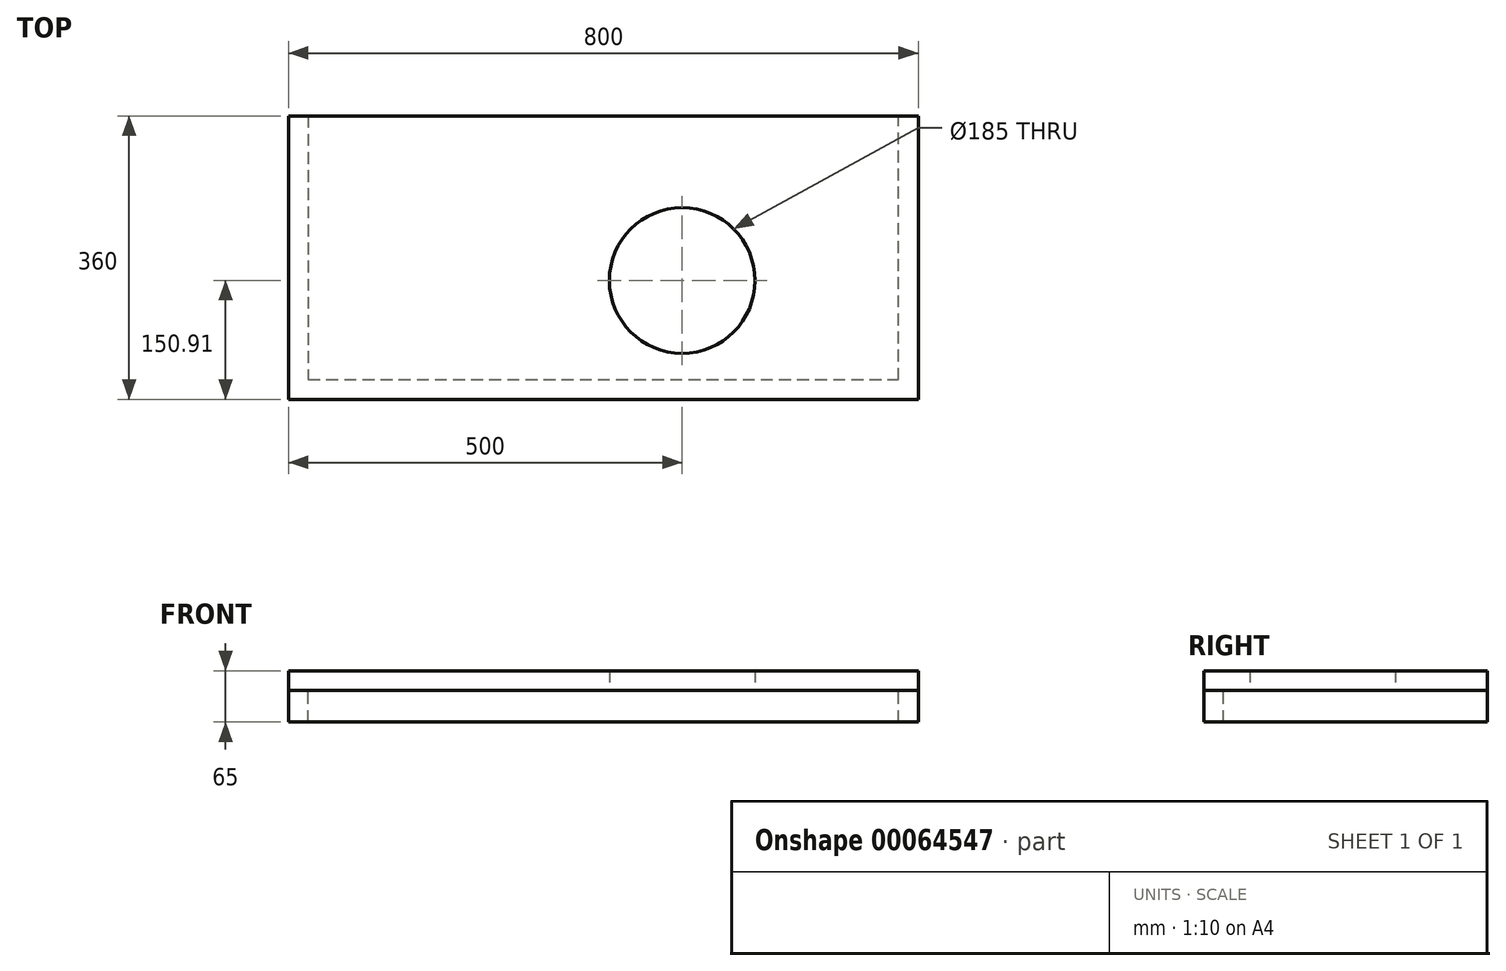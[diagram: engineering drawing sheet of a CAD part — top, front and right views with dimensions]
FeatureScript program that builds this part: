
annotation { "Feature Type Name" : "Feature", "Feature Type Description" : "" }
export const myFeature = defineFeature(function(context is Context, id is Id, definition is map)
    precondition{}
    {
        {
            var Q0;
            Q0=qCreatedBy(makeId("Top.planeOp"),FACE);
            var sketch = newSketch(context, id + "F0", { "sketchPlane" : qUnion([Q0])});
            skLineSegment(sketch, "E0.bottom", {"start": v(0, 0) * mm, "end": v(800, 0) * mm});
            skLineSegment(sketch, "E0.top", {"start": v(0, -360) * mm, "end": v(800, -360) * mm});
            skLineSegment(sketch, "E0.left", {"start": v(0, 0) * mm, "end": v(0, -360) * mm});
            skLineSegment(sketch, "E0.right", {"start": v(800, 0) * mm, "end": v(800, -360) * mm});
            skCircle(sketch, "E1", {"center": v(500, -209.1) * mm, "radius": 92.5 * mm});
            skSolve(sketch);
        }
        {
            var Q0;
            Q0=makeQuery(id+"F0.imprint","IMPRINT",FACE,{"disambiguationData":[TD([[makeQuery(id+"F0.imprint","IMPRINT",EDGE,{"derivedFrom":sQuery(id+"F0.wireOp",EDGE,"E0.bottom")}),-1.0]])]});
            extrude(context, id + "F1", {"entities" : qUnion([Q0]), "depth" : 25 * mm});
        }
        {
            var Q0;
            Q0=makeQuery(id+"F1.opExtrude","CAP_FACE",FACE,{"disambiguationData":[OSD([sQuery(id+"F0.wireOp",EDGE,"E0.bottom"),sQuery(id+"F0.wireOp",EDGE,"E0.top"),sQuery(id+"F0.wireOp",EDGE,"E0.left"),sQuery(id+"F0.wireOp",EDGE,"E0.right"),sQuery(id+"F0.wireOp",EDGE,"E1")])],"isStart":true});
            var sketch = newSketch(context, id + "F2", { "sketchPlane" : qUnion([Q0])});
            skLineSegment(sketch, "E2", {"start": v(25, 0) * mm, "end": v(25, 335) * mm});
            skLineSegment(sketch, "E3", {"start": v(25, 335) * mm, "end": v(775, 335) * mm});
            skLineSegment(sketch, "E4", {"start": v(775, 335) * mm, "end": v(775, 0) * mm});
            skSolve(sketch);
        }
        {
            var Q0;
            {var subQ1=sQuery(id+"F2.wireOp",EDGE,"E2");Q0=makeQuery(id+"F2.imprint","IMPRINT",FACE,{"disambiguationData":[TD([[makeQuery(id+"F2.imprint","IMPRINT",EDGE,{"derivedFrom":subQ1}),1.0]])]});}
            extrude(context, id + "F3", {"entities" : qUnion([Q0]), "depth" : 40 * mm});
        }
    });
